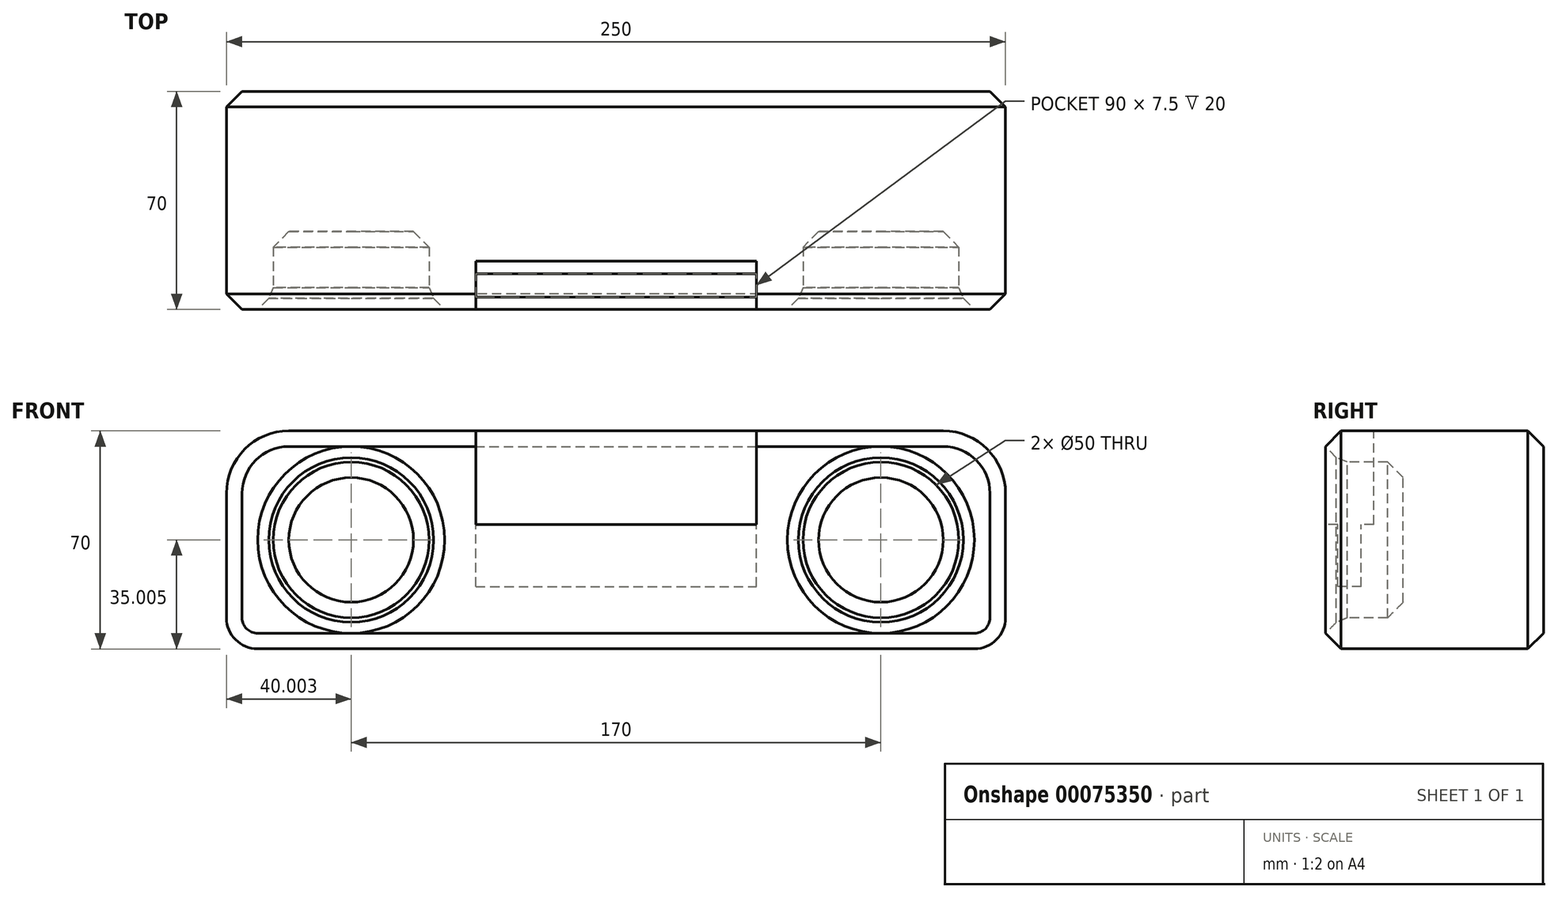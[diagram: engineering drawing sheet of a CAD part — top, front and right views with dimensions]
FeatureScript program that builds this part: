
annotation { "Feature Type Name" : "Feature", "Feature Type Description" : "" }
export const myFeature = defineFeature(function(context is Context, id is Id, definition is map)
    precondition{}
    {
        {
            var Q0;
            Q0=qCreatedBy(makeId("Front.planeOp"),FACE);
            var sketch = newSketch(context, id + "F0", { "sketchPlane" : qUnion([Q0])});
            skLineSegment(sketch, "E0.bottom", {"start": v(-179.72, 46.55) * mm, "end": v(30.28, 46.55) * mm});
            skLineSegment(sketch, "E0.top", {"start": v(-189.72, -23.45) * mm, "end": v(40.28, -23.45) * mm});
            skLineSegment(sketch, "E0.left", {"start": v(-199.72, 26.55) * mm, "end": v(-199.72, -13.45) * mm});
            skLineSegment(sketch, "E0.right", {"start": v(50.28, 26.55) * mm, "end": v(50.28, -13.45) * mm});
            skPoint(sketch, "E1.visualSharp", {"position": v(-199.72, 46.55) * mm});
            skArc(sketch, "E1.filletArc", {"start": v(-179.72, 46.55) * mm, "mid": v(-193.86, 40.7) * mm, "end": v(-199.72, 26.55) * mm});
            skPoint(sketch, "E2.visualSharp", {"position": v(50.28, 46.55) * mm});
            skArc(sketch, "E2.filletArc", {"start": v(50.28, 26.55) * mm, "mid": v(44.42, 40.7) * mm, "end": v(30.28, 46.55) * mm});
            skPoint(sketch, "E3.visualSharp", {"position": v(-199.72, -23.45) * mm});
            skArc(sketch, "E3.filletArc", {"start": v(-199.72, -13.45) * mm, "mid": v(-196.79, -20.52) * mm, "end": v(-189.72, -23.45) * mm});
            skPoint(sketch, "E4.visualSharp", {"position": v(50.28, -23.45) * mm});
            skArc(sketch, "E4.filletArc", {"start": v(40.28, -23.45) * mm, "mid": v(47.35, -20.52) * mm, "end": v(50.28, -13.45) * mm});
            skSolve(sketch);
        }
        {
            var Q0;
            Q0 = qSketchRegion(id + "F0", true);
            extrude(context, id + "F1", {"entities" : qUnion([Q0]), "depth" : 70 * mm});
        }
        {
            var Q0;
            Q0=makeQuery(id+"F1.opExtrude","CAP_FACE",FACE,{"disambiguationData":[OSD([sQuery(id+"F0.wireOp",EDGE,"E0.bottom"),sQuery(id+"F0.wireOp",EDGE,"E0.top"),sQuery(id+"F0.wireOp",EDGE,"E0.left"),sQuery(id+"F0.wireOp",EDGE,"E0.right"),sQuery(id+"F0.wireOp",EDGE,"E1.filletArc"),sQuery(id+"F0.wireOp",EDGE,"E2.filletArc"),sQuery(id+"F0.wireOp",EDGE,"E3.filletArc"),sQuery(id+"F0.wireOp",EDGE,"E4.filletArc")])],"isStart":false});
            var sketch = newSketch(context, id + "F2", { "sketchPlane" : qUnion([Q0])});
            skCircle(sketch, "E5", {"center": v(-159.72, 11.55) * mm, "radius": 25 * mm});
            skCircle(sketch, "E6", {"center": v(10.28, 11.55) * mm, "radius": 25 * mm});
            skSolve(sketch);
        }
        {
            var Q0;
            Q0=makeQuery(id+"F2.imprint","IMPRINT",FACE,{"disambiguationData":[TD([[makeQuery(id+"F2.imprint","IMPRINT",EDGE,{"derivedFrom":sQuery(id+"F2.wireOp",EDGE,"E5")}),1.0]])]});
            var Q1;
            Q1=makeQuery(id+"F2.imprint","IMPRINT",FACE,{"disambiguationData":[TD([[makeQuery(id+"F2.imprint","IMPRINT",EDGE,{"derivedFrom":sQuery(id+"F2.wireOp",EDGE,"E6")}),1.0]])]});
            extrude(context, id + "F3", {"entities" : qUnion([Q0, Q1]), "operationType" : NewBodyOperationType.REMOVE, "oppositeDirection" : true, "depth" : 25 * mm});
        }
        {
            var Q0;
            Q0=makeQuery(id+"F1.opExtrude","CAP_FACE",FACE,{"disambiguationData":[OSD([sQuery(id+"F0.wireOp",EDGE,"E0.bottom"),sQuery(id+"F0.wireOp",EDGE,"E0.top"),sQuery(id+"F0.wireOp",EDGE,"E0.left"),sQuery(id+"F0.wireOp",EDGE,"E0.right"),sQuery(id+"F0.wireOp",EDGE,"E1.filletArc"),sQuery(id+"F0.wireOp",EDGE,"E2.filletArc"),sQuery(id+"F0.wireOp",EDGE,"E3.filletArc"),sQuery(id+"F0.wireOp",EDGE,"E4.filletArc")])],"isStart":false});
            var Q1;
            Q1=makeQuery(id+"F1.opExtrude","SWEPT_FACE",FACE,{"disambiguationData":[OSD([sQuery(id+"F0.wireOp",EDGE,"E3.filletArc")])]});
            var Q2;
            Q2=makeQuery(id+"F1.opExtrude","SWEPT_FACE",FACE,{"disambiguationData":[OSD([sQuery(id+"F0.wireOp",EDGE,"E0.left")])]});
            chamfer(context, id + "F4", {"entities" : qUnion([Q0, Q1, Q2]), "width" : 5 * mm, "tangentPropagation" : true});
        }
        {
            var Q0;
            Q0=makeQuery(id+"F1.opExtrude","SWEPT_FACE",FACE,{"disambiguationData":[OSD([sQuery(id+"F0.wireOp",EDGE,"E0.bottom")])]});
            var sketch = newSketch(context, id + "F5", { "sketchPlane" : qUnion([Q0])});
            skLineSegment(sketch, "E7.bottom", {"start": v(-119.72, -54.5) * mm, "end": v(-29.72, -54.5) * mm});
            skLineSegment(sketch, "E7.top", {"start": v(-119.72, -70) * mm, "end": v(-29.72, -70) * mm});
            skLineSegment(sketch, "E7.left", {"start": v(-119.72, -54.5) * mm, "end": v(-119.72, -70) * mm});
            skLineSegment(sketch, "E7.right", {"start": v(-29.72, -54.5) * mm, "end": v(-29.72, -70) * mm});
            skSolve(sketch);
        }
        {
            var Q0;
            {var subQ0=sQuery(id+"F5.wireOp",EDGE,"E7.bottom");Q0=makeQuery(id+"F5.imprint","IMPRINT",FACE,{"disambiguationData":[TD([[makeQuery(id+"F5.imprint","IMPRINT",EDGE,{"derivedFrom":subQ0}),-1.0]])]});}
            var Q1;
            {var subQ0=sQuery(id+"F5.wireOp",EDGE,"E7.top");Q1=makeQuery(id+"F5.imprint","IMPRINT",FACE,{"disambiguationData":[TD([[makeQuery(id+"F5.imprint","IMPRINT",EDGE,{"derivedFrom":subQ0}),1.0]])]});}
            extrude(context, id + "F6", {"entities" : qUnion([Q0, Q1]), "operationType" : NewBodyOperationType.REMOVE, "oppositeDirection" : true, "depth" : 30 * mm});
        }
        {
            var Q0;
            Q0=makeQuery(id+"F6.boolean.opBoolean","COPY",FACE,{"derivedFrom":makeQuery(id+"F6.opExtrude","CAP_FACE",FACE,{"disambiguationData":[OSD([sQuery(id+"F5.wireOp",EDGE,"E7.bottom"),sQuery(id+"F5.wireOp",EDGE,"E7.top"),sQuery(id+"F5.wireOp",EDGE,"E7.left"),sQuery(id+"F5.wireOp",EDGE,"E7.right")])],"isStart":false})});
            var sketch = newSketch(context, id + "F7", { "sketchPlane" : qUnion([Q0])});
            skLineSegment(sketch, "E8.bottom", {"start": v(-119.72, -66) * mm, "end": v(-29.72, -66) * mm});
            skLineSegment(sketch, "E8.top", {"start": v(-119.72, -58.5) * mm, "end": v(-29.72, -58.5) * mm});
            skLineSegment(sketch, "E8.left", {"start": v(-119.72, -66) * mm, "end": v(-119.72, -58.5) * mm});
            skLineSegment(sketch, "E8.right", {"start": v(-29.72, -66) * mm, "end": v(-29.72, -58.5) * mm});
            skSolve(sketch);
        }
        {
            var Q0;
            Q0=makeQuery(id+"F7.imprint","IMPRINT",FACE,{"disambiguationData":[TD([[makeQuery(id+"F7.imprint","IMPRINT",EDGE,{"derivedFrom":sQuery(id+"F7.wireOp",EDGE,"E8.bottom")}),1.0]])]});
            extrude(context, id + "F8", {"entities" : qUnion([Q0]), "operationType" : NewBodyOperationType.REMOVE, "oppositeDirection" : true, "depth" : 20 * mm});
        }
        {
            var Q0;
            {var subQ0=sQuery(id+"F2.wireOp",EDGE,"E5");Q0=makeQuery(id+"F4.opChamfer","BLEND_EDGE",EDGE,{"blendedFrom":[makeQuery(id+"F3.boolean.opBoolean","COPY",EDGE,{"derivedFrom":makeQuery(id+"F3.opExtrude","CAP_EDGE",EDGE,{"disambiguationData":[OSD([subQ0])],"isStart":true})}),makeQuery(id+"F3.boolean.opBoolean","COPY",FACE,{"derivedFrom":makeQuery(id+"F3.opExtrude","SWEPT_FACE",FACE,{"disambiguationData":[OSD([subQ0])]})})],"blendedInto":[makeQuery(id+"F3.boolean.opBoolean","COPY",FACE,{"derivedFrom":makeQuery(id+"F3.opExtrude","SWEPT_FACE",FACE,{"disambiguationData":[OSD([subQ0])]})})]});}
            var Q1;
            Q1=makeQuery(id+"F3.boolean.opBoolean","COPY",FACE,{"derivedFrom":makeQuery(id+"F3.opExtrude","SWEPT_FACE",FACE,{"disambiguationData":[OSD([sQuery(id+"F2.wireOp",EDGE,"E5")])]})});
            var Q2;
            {var subQ0=sQuery(id+"F2.wireOp",EDGE,"E6");Q2=makeQuery(id+"F4.opChamfer","BLEND_EDGE",EDGE,{"blendedFrom":[makeQuery(id+"F3.boolean.opBoolean","COPY",EDGE,{"derivedFrom":makeQuery(id+"F3.opExtrude","CAP_EDGE",EDGE,{"disambiguationData":[OSD([subQ0])],"isStart":true})}),makeQuery(id+"F3.boolean.opBoolean","COPY",FACE,{"derivedFrom":makeQuery(id+"F3.opExtrude","SWEPT_FACE",FACE,{"disambiguationData":[OSD([subQ0])]})})],"blendedInto":[makeQuery(id+"F3.boolean.opBoolean","COPY",FACE,{"derivedFrom":makeQuery(id+"F3.opExtrude","SWEPT_FACE",FACE,{"disambiguationData":[OSD([subQ0])]})})]});}
            var Q3;
            Q3=makeQuery(id+"F3.boolean.opBoolean","COPY",FACE,{"derivedFrom":makeQuery(id+"F3.opExtrude","SWEPT_FACE",FACE,{"disambiguationData":[OSD([sQuery(id+"F2.wireOp",EDGE,"E6")])]})});
            chamfer(context, id + "F9", {"entities" : qUnion([Q0, Q1, Q2, Q3]), "width" : 5 * mm, "tangentPropagation" : true});
        }
    });
